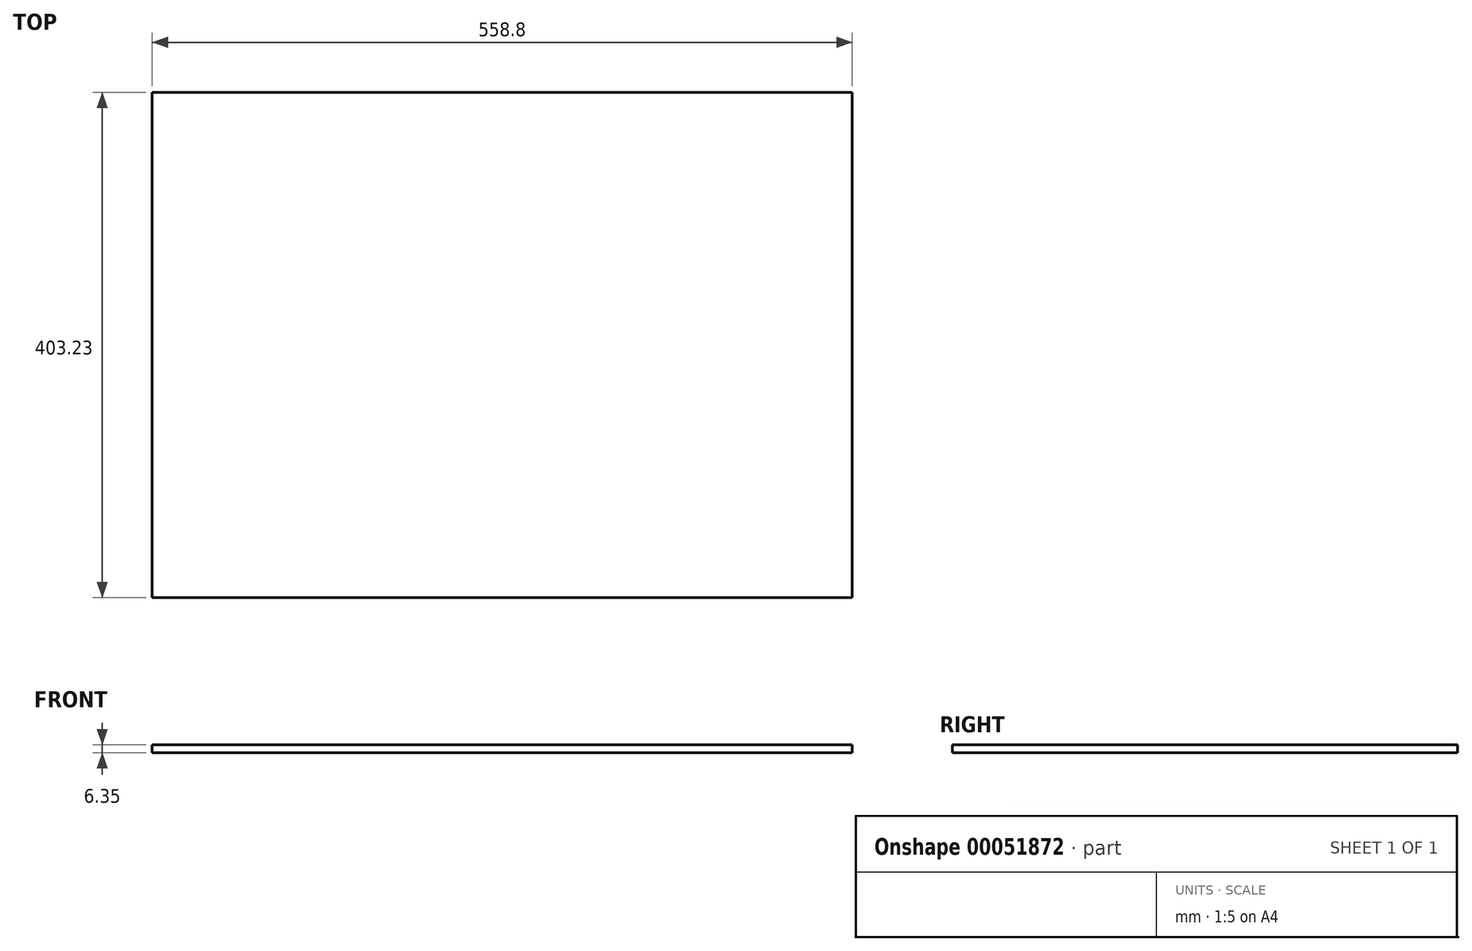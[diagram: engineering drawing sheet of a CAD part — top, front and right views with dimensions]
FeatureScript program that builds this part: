
annotation { "Feature Type Name" : "Feature", "Feature Type Description" : "" }
export const myFeature = defineFeature(function(context is Context, id is Id, definition is map)
    precondition{}
    {
        {
            var Q0;
            Q0=qCreatedBy(makeId("Top.planeOp"),FACE);
            var sketch = newSketch(context, id + "F0", { "sketchPlane" : qUnion([Q0])});
            skLineSegment(sketch, "E0.bottom", {"start": v(-254, 203.2) * mm, "end": v(304.8, 203.2) * mm});
            skLineSegment(sketch, "E0.top", {"start": v(-254, -200.02) * mm, "end": v(304.8, -200.02) * mm});
            skLineSegment(sketch, "E0.left", {"start": v(-254, 203.2) * mm, "end": v(-254, -200.02) * mm});
            skLineSegment(sketch, "E0.right", {"start": v(304.8, 203.2) * mm, "end": v(304.8, -200.02) * mm});
            skSolve(sketch);
        }
        {
            var Q0;
            Q0=makeQuery(id+"F0.imprint","IMPRINT",FACE,{"disambiguationData":[TD([[makeQuery(id+"F0.imprint","IMPRINT",EDGE,{"derivedFrom":sQuery(id+"F0.wireOp",EDGE,"E0.bottom")}),-1.0]])]});
            extrude(context, id + "F1", {"entities" : qUnion([Q0]), "depth" : 6.35 * mm});
        }
    });
